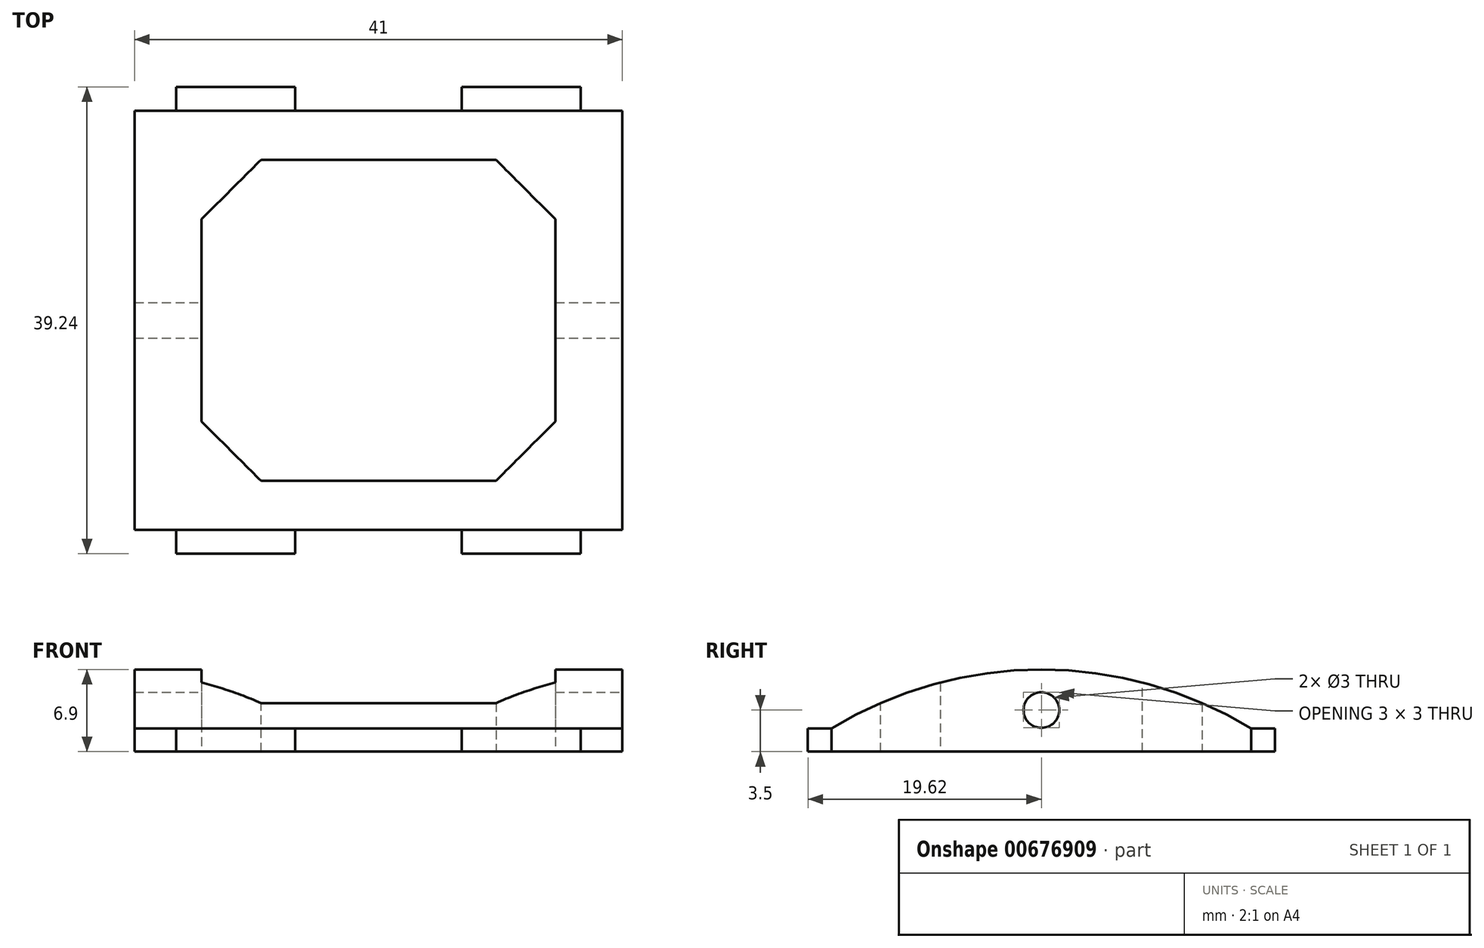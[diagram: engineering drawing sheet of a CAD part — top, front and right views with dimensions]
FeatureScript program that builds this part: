
annotation { "Feature Type Name" : "Feature", "Feature Type Description" : "" }
export const myFeature = defineFeature(function(context is Context, id is Id, definition is map)
    precondition{}
    {
        {
            var Q0;
            Q0=qCreatedBy(makeId("Top.planeOp"),FACE);
            var sketch = newSketch(context, id + "F0", { "sketchPlane" : qUnion([Q0])});
            skLineSegment(sketch, "E0.bottom", {"start": v(-20.5, 19.63) * mm, "end": v(20.5, 19.63) * mm});
            skLineSegment(sketch, "E0.top", {"start": v(-20.5, -19.62) * mm, "end": v(20.5, -19.62) * mm});
            skLineSegment(sketch, "E0.left", {"start": v(-20.5, 19.63) * mm, "end": v(-20.5, -19.62) * mm});
            skLineSegment(sketch, "E0.right", {"start": v(20.5, 19.63) * mm, "end": v(20.5, -19.62) * mm});
            skPoint(sketch, "E0.middle", {"position": v(0, 0) * mm});
            skLineSegment(sketch, "E1", {"start": v(-20.5, 17.62) * mm, "end": v(-17, 17.62) * mm});
            skLineSegment(sketch, "E2", {"start": v(-17, 17.62) * mm, "end": v(-17, 19.63) * mm});
            skLineSegment(sketch, "E3", {"start": v(-7, 19.63) * mm, "end": v(-7, 17.63) * mm});
            skLineSegment(sketch, "E4", {"start": v(-7, 17.63) * mm, "end": v(7, 17.63) * mm});
            skLineSegment(sketch, "E5", {"start": v(7, 17.63) * mm, "end": v(7, 19.63) * mm});
            skLineSegment(sketch, "E6", {"start": v(17, 19.63) * mm, "end": v(17, 17.63) * mm});
            skLineSegment(sketch, "E7", {"start": v(17, 17.63) * mm, "end": v(20.5, 17.63) * mm});
            skLineSegment(sketch, "E8", {"start": v(-20.5, 0) * mm, "end": v(20.5, 0) * mm, "construction": true});
            skLineSegment(sketch, "E9.MirrorCS", {"start": v(-20.5, -17.62) * mm, "end": v(-17, -17.62) * mm});
            skLineSegment(sketch, "E10.MirrorCS", {"start": v(-17, -17.62) * mm, "end": v(-17, -19.62) * mm});
            skLineSegment(sketch, "E11.MirrorCS", {"start": v(-7, -19.62) * mm, "end": v(-7, -17.62) * mm});
            skLineSegment(sketch, "E12.MirrorCS", {"start": v(-7, -17.62) * mm, "end": v(7, -17.62) * mm});
            skLineSegment(sketch, "E13.MirrorCS", {"start": v(7, -17.62) * mm, "end": v(7, -19.62) * mm});
            skLineSegment(sketch, "E14.MirrorCS", {"start": v(17, -19.62) * mm, "end": v(17, -17.62) * mm});
            skLineSegment(sketch, "E15.MirrorCS", {"start": v(17, -17.62) * mm, "end": v(20.5, -17.62) * mm});
            skSolve(sketch);
        }
        {
            var Q0;
            {var subQ1=sQuery(id+"F0.wireOp",EDGE,"E1");Q0=makeQuery(id+"F0.imprint","IMPRINT",FACE,{"disambiguationData":[TD([[makeQuery(id+"F0.imprint","IMPRINT",EDGE,{"derivedFrom":subQ1}),-1.0]])]});}
            extrude(context, id + "F1", {"entities" : qUnion([Q0]), "depth" : 1.95 * mm, "offsetDistance" : 25 * mm});
        }
        {
            var Q0;
            Q0=makeQuery(id+"F1.opExtrude","SWEPT_FACE",FACE,{"disambiguationData":[OSD([sQuery(id+"F0.wireOp",EDGE,"E0.right")])]});
            var sketch = newSketch(context, id + "F2", { "sketchPlane" : qUnion([Q0])});
            skCircle(sketch, "E16", {"center": v(0, 3.5) * mm, "radius": 1.5 * mm});
            skArc(sketch, "E17", {"start": v(17.63, 1.95) * mm, "mid": v(0, 6.9) * mm, "end": v(-17.62, 1.95) * mm});
            skSolve(sketch);
        }
        {
            var Q0;
            Q0=makeQuery(id+"F2.imprint","IMPRINT",FACE,{"disambiguationData":[TD([[makeQuery(id+"F2.imprint","IMPRINT",EDGE,{"derivedFrom":sQuery(id+"F2.wireOp",EDGE,"E16")}),-1.0]])]});
            var Q1;
            Q1=makeQuery(id+"F1.opExtrude","SWEPT_FACE",FACE,{"disambiguationData":[OSD([sQuery(id+"F0.wireOp",EDGE,"E0.left")])]});
            extrude(context, id + "F3", {"entities" : qUnion([Q0]), "operationType" : NewBodyOperationType.ADD, "endBound" : BoundingType.UP_TO_SURFACE, "oppositeDirection" : true, "depth" : 25 * mm, "endBoundEntityFace" : qUnion([Q1]), "offsetDistance" : 25 * mm});
        }
        {
            var Q0;
            Q0=makeQuery(id+"F1.opExtrude","CAP_FACE",FACE,{"disambiguationData":[OSD([sQuery(id+"F0.wireOp",EDGE,"E0.bottom"),sQuery(id+"F0.wireOp",EDGE,"E0.top"),sQuery(id+"F0.wireOp",EDGE,"E0.left"),sQuery(id+"F0.wireOp",EDGE,"E0.right"),sQuery(id+"F0.wireOp",EDGE,"E1"),sQuery(id+"F0.wireOp",EDGE,"E2"),sQuery(id+"F0.wireOp",EDGE,"E3"),sQuery(id+"F0.wireOp",EDGE,"E4"),sQuery(id+"F0.wireOp",EDGE,"E5"),sQuery(id+"F0.wireOp",EDGE,"E6"),sQuery(id+"F0.wireOp",EDGE,"E7"),sQuery(id+"F0.wireOp",EDGE,"E9.MirrorCS"),sQuery(id+"F0.wireOp",EDGE,"E10.MirrorCS"),sQuery(id+"F0.wireOp",EDGE,"E11.MirrorCS"),sQuery(id+"F0.wireOp",EDGE,"E12.MirrorCS"),sQuery(id+"F0.wireOp",EDGE,"E13.MirrorCS"),sQuery(id+"F0.wireOp",EDGE,"E14.MirrorCS"),sQuery(id+"F0.wireOp",EDGE,"E15.MirrorCS")])],"isStart":true});
            var sketch = newSketch(context, id + "F4", { "sketchPlane" : qUnion([Q0])});
            skLineSegment(sketch, "E18.bottom", {"start": v(-14.88, 13.5) * mm, "end": v(14.88, 13.5) * mm});
            skLineSegment(sketch, "E18.top", {"start": v(-14.88, -13.5) * mm, "end": v(14.88, -13.5) * mm});
            skLineSegment(sketch, "E18.left", {"start": v(-14.88, 13.5) * mm, "end": v(-14.88, -13.5) * mm});
            skLineSegment(sketch, "E18.right", {"start": v(14.88, 13.5) * mm, "end": v(14.88, -13.5) * mm});
            skPoint(sketch, "E18.middle", {"position": v(0, 0) * mm});
            skSolve(sketch);
        }
        {
            var Q0;
            Q0=makeQuery(id+"F4.imprint","IMPRINT",FACE,{"disambiguationData":[TD([[makeQuery(id+"F4.imprint","IMPRINT",EDGE,{"derivedFrom":sQuery(id+"F4.wireOp",EDGE,"E18.bottom")}),-1.0]])]});
            extrude(context, id + "F5", {"entities" : qUnion([Q0]), "operationType" : NewBodyOperationType.REMOVE, "endBound" : BoundingType.THROUGH_ALL, "oppositeDirection" : true, "depth" : 25 * mm, "offsetDistance" : 25 * mm});
        }
        {
            var Q0;
            Q0=makeQuery(id+"F5.boolean.opBoolean","COPY",EDGE,{"derivedFrom":makeQuery(id+"F5.opExtrude","SWEPT_EDGE",EDGE,{"disambiguationData":[OSD([sQuery(id+"F4.wireOp",EDGE,"E18.bottom"),sQuery(id+"F4.wireOp",EDGE,"E18.right")])]})});
            var Q1;
            Q1=makeQuery(id+"F5.boolean.opBoolean","COPY",EDGE,{"derivedFrom":makeQuery(id+"F5.opExtrude","SWEPT_EDGE",EDGE,{"disambiguationData":[OSD([sQuery(id+"F4.wireOp",EDGE,"E18.bottom"),sQuery(id+"F4.wireOp",EDGE,"E18.left")])]})});
            var Q2;
            Q2=makeQuery(id+"F5.boolean.opBoolean","COPY",EDGE,{"derivedFrom":makeQuery(id+"F5.opExtrude","SWEPT_EDGE",EDGE,{"disambiguationData":[OSD([sQuery(id+"F4.wireOp",EDGE,"E18.top"),sQuery(id+"F4.wireOp",EDGE,"E18.right")])]})});
            var Q3;
            Q3=makeQuery(id+"F5.boolean.opBoolean","COPY",EDGE,{"derivedFrom":makeQuery(id+"F5.opExtrude","SWEPT_EDGE",EDGE,{"disambiguationData":[OSD([sQuery(id+"F4.wireOp",EDGE,"E18.top"),sQuery(id+"F4.wireOp",EDGE,"E18.left")])]})});
            chamfer(context, id + "F6", {"entities" : qUnion([Q0, Q1, Q2, Q3]), "width" : 5 * mm, "tangentPropagation" : true});
        }
    });
